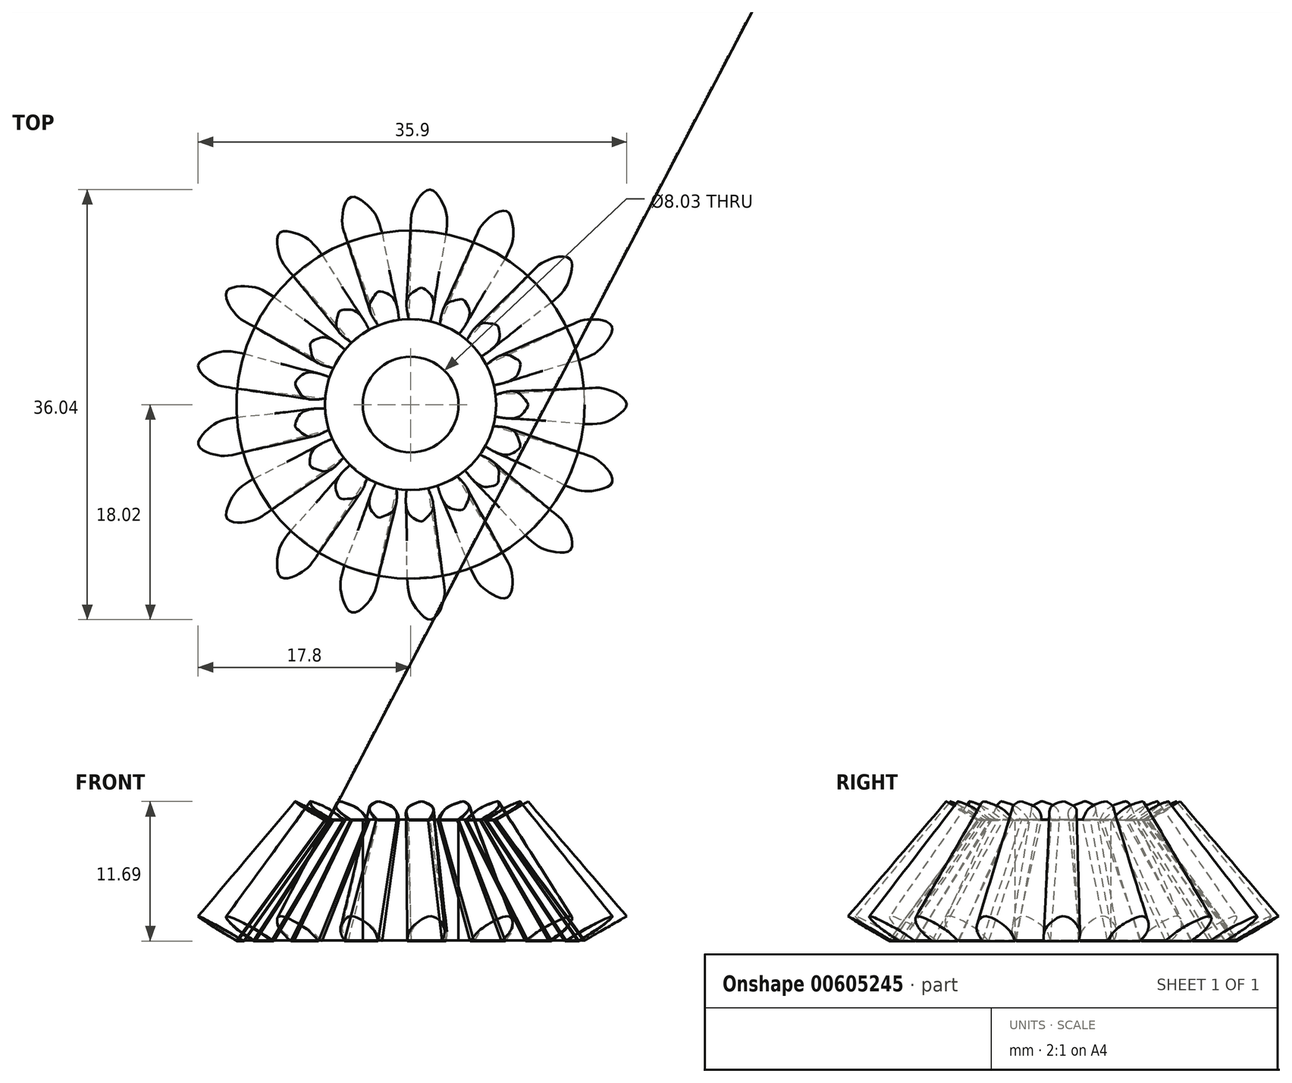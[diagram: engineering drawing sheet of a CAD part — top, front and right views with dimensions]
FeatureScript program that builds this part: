
annotation { "Feature Type Name" : "Feature", "Feature Type Description" : "" }
export const myFeature = defineFeature(function(context is Context, id is Id, definition is map)
    precondition{}
    {
        {
            var Q0;
            Q0=qCreatedBy(makeId("Top.planeOp"),FACE);
            var sketch = newSketch(context, id + "F0", { "sketchPlane" : qUnion([Q0])});
            skCircle(sketch, "E0", {"center": v(0, 0) * mm, "radius": 14.59 * mm});
            skSolve(sketch);
        }
        {
            var Q0;
            Q0=qCreatedBy(makeId("Top.planeOp"),FACE);
            cPlane(context, id + "F1", {"entities" : qUnion([Q0]), "cplaneType" : CPlaneType.OFFSET, "offset" : 10.12 * mm, "width" : 150 * mm, "height" : 150 * mm});
        }
        {
            var Q0;
            Q0=qCreatedBy(id+"F1.planeOp",FACE);
            var sketch = newSketch(context, id + "F2", { "sketchPlane" : qUnion([Q0])});
            skCircle(sketch, "E1", {"center": v(0, 0) * mm, "radius": 7.16 * mm});
            skSolve(sketch);
        }
        {
            var Q0;
            Q0=makeQuery(id+"F0.imprint","IMPRINT",FACE,{"disambiguationData":[TD([[makeQuery(id+"F0.imprint","IMPRINT",EDGE,{"derivedFrom":sQuery(id+"F0.wireOp",EDGE,"E0")}),1.0]])]});
            var Q1;
            Q1=makeQuery(id+"F2.imprint","IMPRINT",FACE,{"disambiguationData":[TD([[makeQuery(id+"F2.imprint","IMPRINT",EDGE,{"derivedFrom":sQuery(id+"F2.wireOp",EDGE,"E1")}),1.0]])]});
            loft(context, id + "F3", {"sheetProfilesArray" : [{ "sheetProfileEntities" : qUnion([Q0]) }, { "sheetProfileEntities" : qUnion([Q1]) }]});
        }
        {
            var Q0;
            Q0=qCreatedBy(id+"F1.planeOp",FACE);
            var sketch = newSketch(context, id + "F4", { "sketchPlane" : qUnion([Q0])});
            skCircle(sketch, "E2", {"center": v(0, 0) * mm, "radius": 4.01 * mm});
            skSolve(sketch);
        }
        {
            var Q0;
            Q0=makeQuery(id+"F4.imprint","IMPRINT",FACE,{"disambiguationData":[TD([[makeQuery(id+"F4.imprint","IMPRINT",EDGE,{"derivedFrom":sQuery(id+"F4.wireOp",EDGE,"E2")}),1.0]])]});
            extrude(context, id + "F5", {"entities" : qUnion([Q0]), "operationType" : NewBodyOperationType.REMOVE, "oppositeDirection" : true, "depth" : 25 * mm, "hasOffset" : true, "offsetDistance" : 25 * mm});
        }
        {
            var Q0;
            Q0=qCreatedBy(makeId("Top.planeOp"),FACE);
            var sketch = newSketch(context, id + "F6", { "sketchPlane" : qUnion([Q0])});
            skLineSegment(sketch, "E3", {"start": v(0, 29.95) * mm, "end": v(0, -35.18) * mm});
            skLineSegment(sketch, "E4", {"start": v(-28.83, 0) * mm, "end": v(40.4, 0) * mm});
            skSolve(sketch);
        }
        {
            var Q0;
            Q0=sQuery(id+"F6.wireOp",EDGE,"E3");
            cPlane(context, id + "F7", {"entities" : qUnion([Q0]), "cplaneType" : CPlaneType.LINE_ANGLE, "offset" : 25 * mm, "angle" : 30 * degree, "width" : 150 * mm, "height" : 150 * mm});
        }
        {
            var Q0;
            Q0=qCreatedBy(id+"F7.planeOp",FACE);
            cPlane(context, id + "F8", {"entities" : qUnion([Q0]), "cplaneType" : CPlaneType.OFFSET, "offset" : 7.3 * mm, "width" : 150 * mm, "height" : 150 * mm});
        }
        {
            var Q0;
            Q0=qCreatedBy(id+"F8.planeOp",FACE);
            cPlane(context, id + "F9", {"entities" : qUnion([Q0]), "cplaneType" : CPlaneType.OFFSET, "offset" : 12.46 * mm, "oppositeDirection" : true, "width" : 150 * mm, "height" : 150 * mm});
        }
        {
            var Q0;
            Q0=qCreatedBy(id+"F8.planeOp",FACE);
            var sketch = newSketch(context, id + "F10", { "sketchPlane" : qUnion([Q0])});
            skFitSpline(sketch, "E5", {"points": [v(12.53, 1.64) * mm, v(14.08, 1.59) * mm, v(15.06, 1.3) * mm, v(16.08, 0.74) * mm, v(16.69, 0) * mm, v(16.11, -0.73) * mm, v(15.06, -1.2) * mm, v(14.08, -1.4) * mm, v(12.53, -1.3) * mm], "startDerivative": vector(11.35, 0.14) * mm, "endDerivative": vector(-11.34, 1.41) * mm});
            skLineSegment(sketch, "E6", {"start": v(12.53, -1.3) * mm, "end": v(12.53, 1.64) * mm});
            skSolve(sketch);
        }
        {
            var Q0;
            Q0=qCreatedBy(id+"F9.planeOp",FACE);
            var sketch = newSketch(context, id + "F11", { "sketchPlane" : qUnion([Q0])});
            skFitSpline(sketch, "E7", {"points": [v(11.2, -0.81) * mm, v(12.63, -1.11) * mm, v(13.48, -0.94) * mm, v(14.03, -0.45) * mm, v(14.34, 0) * mm, v(14.04, 0.54) * mm, v(13.53, 0.98) * mm, v(12.56, 1.16) * mm, v(11.15, 1) * mm], "startDerivative": vector(9.34, -2.62) * mm, "endDerivative": vector(-9.13, -1.5) * mm});
            skLineSegment(sketch, "E8", {"start": v(11.2, -0.81) * mm, "end": v(11.15, 1) * mm});
            skSolve(sketch);
        }
        {
            var Q1;
            Q1 = qSketchRegion(id + "F10", true);
            var Q2;
            Q2 = qSketchRegion(id + "F11", true);
            loft(context, id + "F12", {"sheetProfilesArray" : [{ "sheetProfileEntities" : qUnion([Q1]) }, { "sheetProfileEntities" : qUnion([Q2]) }]});
        }
        {
            var Q0;
            Q0=qCreatedBy(makeId("Front.planeOp"),FACE);
            var sketch = newSketch(context, id + "F13", { "sketchPlane" : qUnion([Q0])});
            skLineSegment(sketch, "E9", {"start": v(0, -38.7) * mm, "end": v(0, 37.92) * mm, "construction": true});
            skSolve(sketch);
        }
        {
            var Q0;
            Q0=makeQuery(id+"F12.opLoft","SWEPT_BODY",BODY,{"disambiguationData":[OSD([makeQuery(id+"F10.imprint","IMPRINT",FACE,{"disambiguationData":[TD([[makeQuery(id+"F10.imprint","IMPRINT",EDGE,{"derivedFrom":sQuery(id+"F10.wireOp",EDGE,"E5")}),-1.0]])]}),makeQuery(id+"F11.imprint","IMPRINT",FACE,{"disambiguationData":[TD([[makeQuery(id+"F11.imprint","IMPRINT",EDGE,{"derivedFrom":sQuery(id+"F11.wireOp",EDGE,"E7")}),1.0]])]})])]});
            var Q1;
            Q1=sQuery(id+"F13.wireOp",EDGE,"E9");
            circularPattern(context, id + "F14", {"entities" : qUnion([Q0]), "axis" : qUnion([Q1]), "angle" : 360 * degree, "instanceCount" : 17, "oppositeDirection" : true, "equalSpace" : true});
        }
    });
